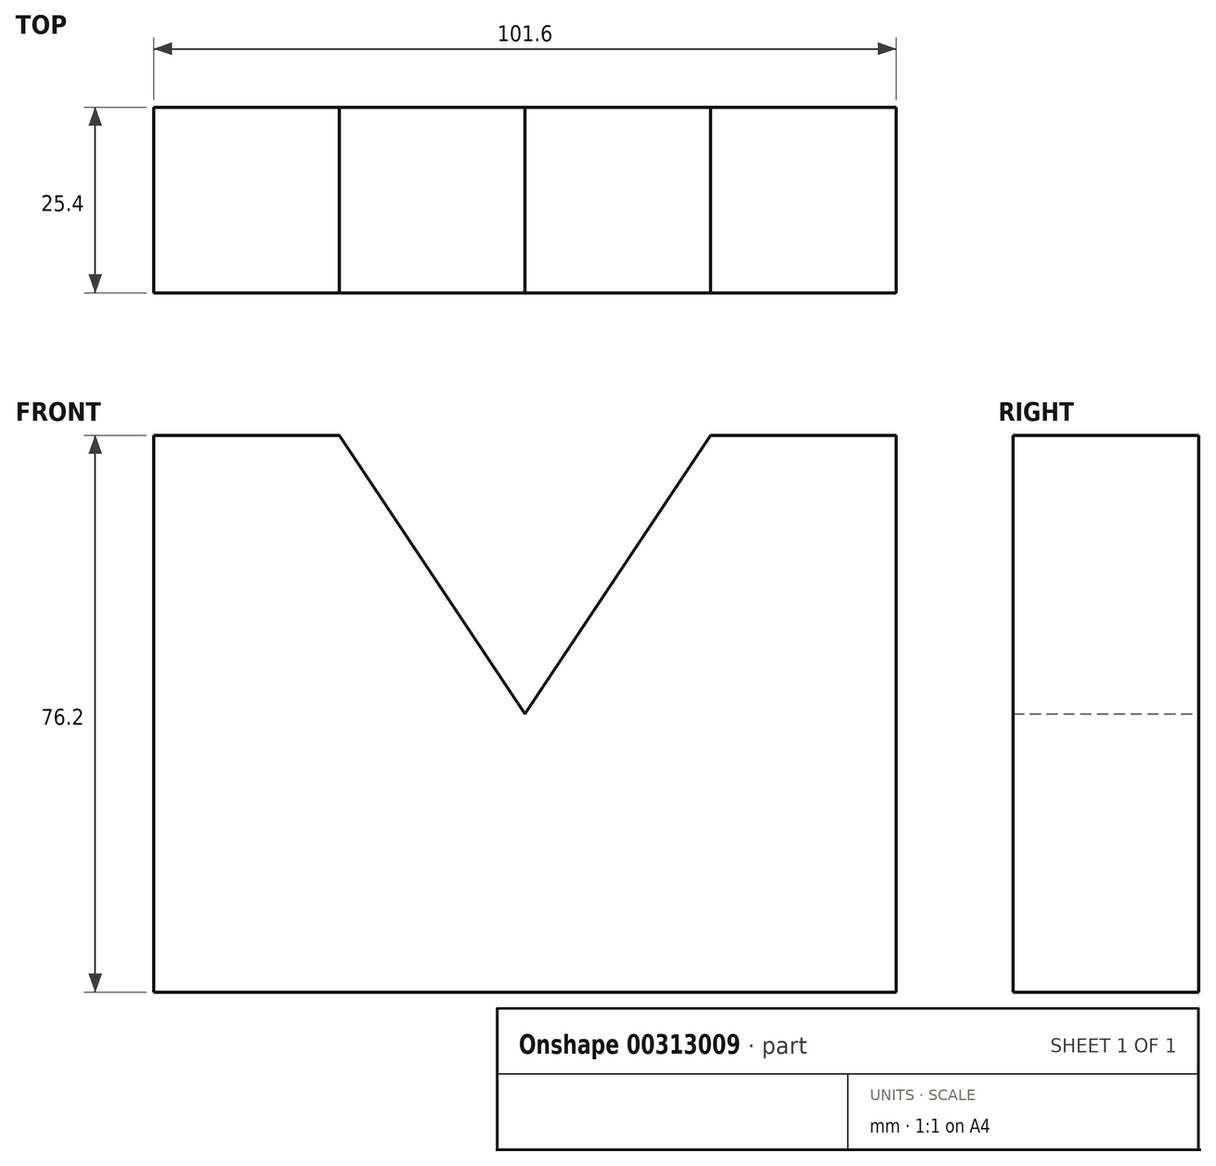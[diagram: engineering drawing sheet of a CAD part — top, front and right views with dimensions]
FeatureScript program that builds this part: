
annotation { "Feature Type Name" : "Feature", "Feature Type Description" : "" }
export const myFeature = defineFeature(function(context is Context, id is Id, definition is map)
    precondition{}
    {
        {
            var Q0;
            Q0=qCreatedBy(makeId("Front.planeOp"),FACE);
            var sketch = newSketch(context, id + "F0", { "sketchPlane" : qUnion([Q0])});
            skLineSegment(sketch, "E0", {"start": v(-44.1, 24.24) * mm, "end": v(-44.1, -51.96) * mm});
            skLineSegment(sketch, "E1", {"start": v(-44.1, -51.96) * mm, "end": v(57.5, -51.96) * mm});
            skLineSegment(sketch, "E2", {"start": v(57.5, -51.96) * mm, "end": v(57.5, 24.24) * mm});
            skLineSegment(sketch, "E3", {"start": v(-44.1, 24.24) * mm, "end": v(-18.7, 24.24) * mm});
            skLineSegment(sketch, "E4", {"start": v(57.5, 24.24) * mm, "end": v(32.1, 24.24) * mm});
            skLineSegment(sketch, "E5", {"start": v(-18.7, 24.24) * mm, "end": v(6.7, -13.86) * mm});
            skLineSegment(sketch, "E6", {"start": v(32.1, 24.24) * mm, "end": v(6.7, -13.86) * mm});
            skSolve(sketch);
        }
        {
            var Q0;
            Q0=makeQuery(id+"F0.imprint","IMPRINT",FACE,{"disambiguationData":[TD([[makeQuery(id+"F0.imprint","IMPRINT",EDGE,{"derivedFrom":sQuery(id+"F0.wireOp",EDGE,"E0")}),1.0]])]});
            extrude(context, id + "F1", {"entities" : qUnion([Q0]), "depth" : 25.4 * mm});
        }
    });
